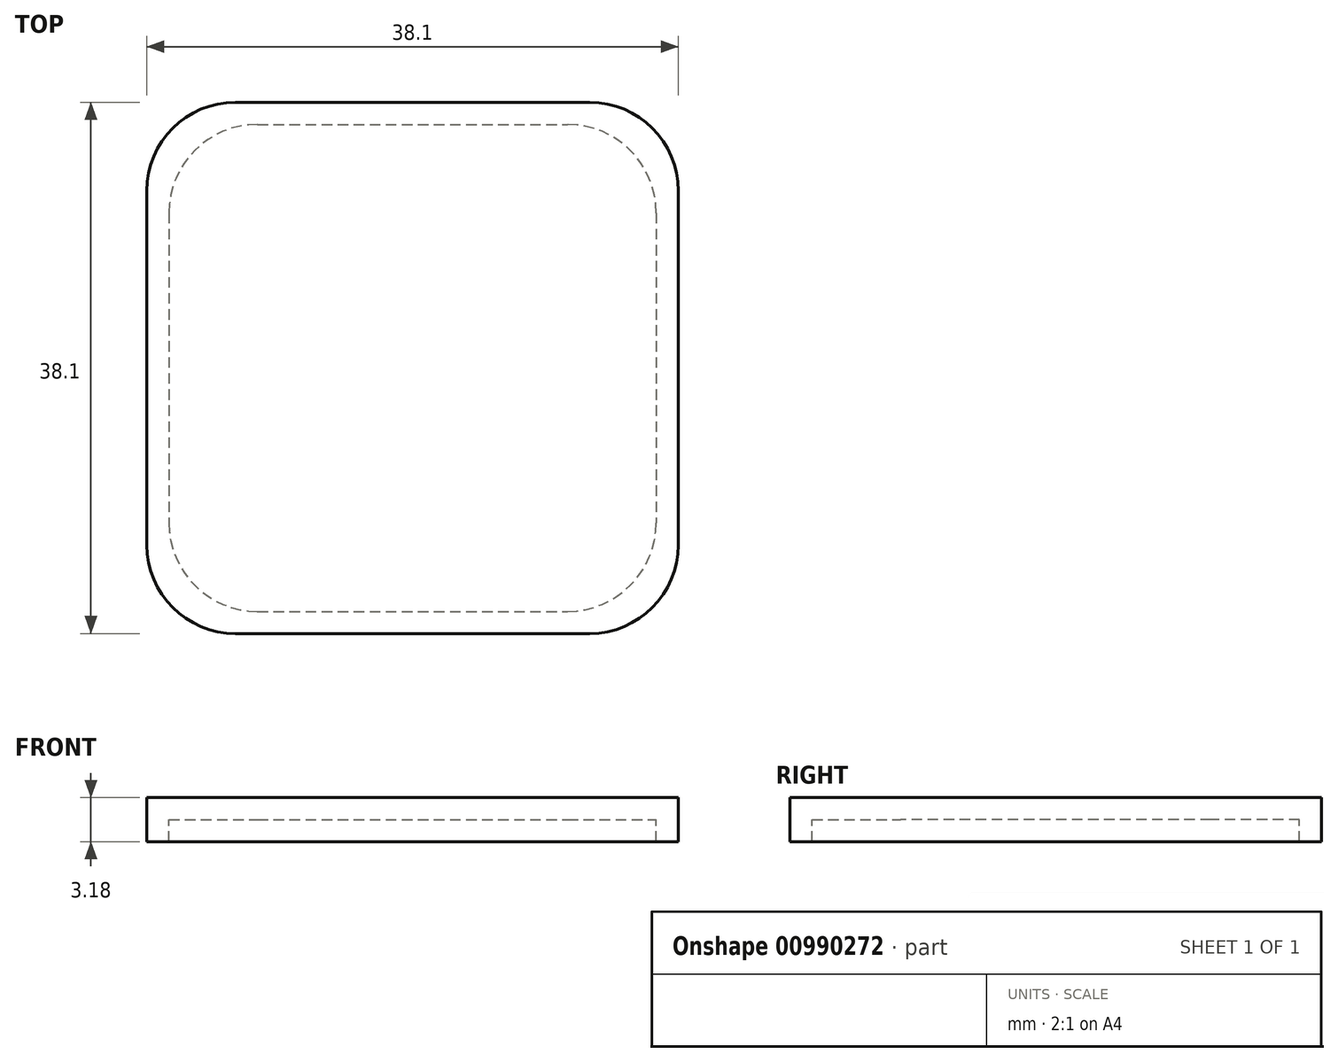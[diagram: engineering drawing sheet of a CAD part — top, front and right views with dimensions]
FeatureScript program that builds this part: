
annotation { "Feature Type Name" : "Feature", "Feature Type Description" : "" }
export const myFeature = defineFeature(function(context is Context, id is Id, definition is map)
    precondition{}
    {
        {
            var Q0;
            Q0=qCreatedBy(makeId("Top.planeOp"),FACE);
            var sketch = newSketch(context, id + "F0", { "sketchPlane" : qUnion([Q0])});
            skLineSegment(sketch, "E0.bottom", {"start": v(15.01, 15.04) * mm, "end": v(40.41, 15.04) * mm});
            skLineSegment(sketch, "E0.top", {"start": v(15.01, -23.06) * mm, "end": v(40.41, -23.06) * mm});
            skLineSegment(sketch, "E0.left", {"start": v(8.66, 8.7) * mm, "end": v(8.66, -16.7) * mm});
            skLineSegment(sketch, "E0.right", {"start": v(46.76, 8.7) * mm, "end": v(46.76, -16.7) * mm});
            skPoint(sketch, "E1.visualSharp", {"position": v(46.76, 15.04) * mm});
            skArc(sketch, "E1.filletArc", {"start": v(46.76, 8.7) * mm, "mid": v(44.9, 13.19) * mm, "end": v(40.41, 15.04) * mm});
            skPoint(sketch, "E2.visualSharp", {"position": v(8.66, 15.04) * mm});
            skArc(sketch, "E2.filletArc", {"start": v(15.01, 15.04) * mm, "mid": v(10.52, 13.19) * mm, "end": v(8.66, 8.7) * mm});
            skPoint(sketch, "E3.visualSharp", {"position": v(8.66, -23.06) * mm});
            skArc(sketch, "E3.filletArc", {"start": v(8.66, -16.7) * mm, "mid": v(10.52, -21.2) * mm, "end": v(15.01, -23.06) * mm});
            skPoint(sketch, "E4.visualSharp", {"position": v(46.76, -23.06) * mm});
            skArc(sketch, "E4.filletArc", {"start": v(40.41, -23.06) * mm, "mid": v(44.9, -21.2) * mm, "end": v(46.76, -16.7) * mm});
            skSolve(sketch);
        }
        {
            var Q0;
            Q0=qSketchRegion(id+"F0",true);
            extrude(context, id + "F1", {"entities" : qUnion([Q0]), "depth" : 1.59 * mm, "offsetDistance" : 25.4 * mm});
        }
        {
            var Q0;
            Q0=makeQuery(id+"F1.opExtrude","CAP_FACE",FACE,{"disambiguationData":[OSD([sQuery(id+"F0.wireOp",EDGE,"E0.bottom"),sQuery(id+"F0.wireOp",EDGE,"E0.top"),sQuery(id+"F0.wireOp",EDGE,"E0.left"),sQuery(id+"F0.wireOp",EDGE,"E0.right"),sQuery(id+"F0.wireOp",EDGE,"E1.filletArc"),sQuery(id+"F0.wireOp",EDGE,"E2.filletArc"),sQuery(id+"F0.wireOp",EDGE,"E3.filletArc"),sQuery(id+"F0.wireOp",EDGE,"E4.filletArc")])],"isStart":false});
            var sketch = newSketch(context, id + "F2", { "sketchPlane" : qUnion([Q0])});
            skLineSegment(sketch, "E5.0", {"start": v(16.6, 13.46) * mm, "end": v(38.82, 13.46) * mm});
            skLineSegment(sketch, "E5.1", {"start": v(10.25, 7.1) * mm, "end": v(10.25, -15.12) * mm});
            skLineSegment(sketch, "E5.2", {"start": v(16.6, -21.47) * mm, "end": v(38.82, -21.47) * mm});
            skLineSegment(sketch, "E5.3", {"start": v(45.17, 7.1) * mm, "end": v(45.17, -15.12) * mm});
            skPoint(sketch, "E6.visualSharp", {"position": v(10.25, -21.47) * mm});
            skArc(sketch, "E6.filletArc", {"start": v(10.25, -15.12) * mm, "mid": v(12.1, -19.6) * mm, "end": v(16.6, -21.47) * mm});
            skPoint(sketch, "E7.visualSharp", {"position": v(45.17, -21.47) * mm});
            skArc(sketch, "E7.filletArc", {"start": v(38.82, -21.47) * mm, "mid": v(43.31, -19.6) * mm, "end": v(45.17, -15.12) * mm});
            skPoint(sketch, "E8.visualSharp", {"position": v(45.17, 13.46) * mm});
            skArc(sketch, "E8.filletArc", {"start": v(45.17, 7.1) * mm, "mid": v(43.31, 11.6) * mm, "end": v(38.82, 13.46) * mm});
            skPoint(sketch, "E9.visualSharp", {"position": v(10.25, 13.46) * mm});
            skArc(sketch, "E9.filletArc", {"start": v(16.6, 13.46) * mm, "mid": v(12.1, 11.6) * mm, "end": v(10.25, 7.1) * mm});
            skSolve(sketch);
        }
        {
            var Q0;
            Q0=makeQuery(id+"F2.imprint","IMPRINT",FACE,{"disambiguationData":[TD([[makeQuery(id+"F2.imprint","IMPRINT",EDGE,{"derivedFrom":sQuery(id+"F2.wireOp",EDGE,"E5.0")}),1.0]])]});
            extrude(context, id + "F3", {"entities" : qUnion([Q0]), "operationType" : NewBodyOperationType.ADD, "oppositeDirection" : true, "depth" : 3.17 * mm, "offsetDistance" : 25.4 * mm});
        }
    });
